# Revit family: Domotics-DomesticRanges-GEWISS-CHORUS_POWER-SOCKET-OUTLET_USA
name_source: partatom
category: Apparecchi elettrici
revit_build: Autodesk Revit 2016 (Build: 20161004_0715(x64)
units: mm (PartAtom-declared; Revit-internal decimal feet)

## family parameters
Condiviso = Sì
Host = Superficie
Mantenere orientamento annotazione = Sì
Punto di calcolo locali = Sì
Quota connettore circolare = Usa diametro
Taglio con vuoti quando caricato = Sì
Tipo di parte = Normale

## types (3) — shared parameters
Breaking capacity: = 1.25 In (100 position changes)
Carico apparente = 0 VA
Catalogue = DOMOTICS
Catalogue Range = CHORUS - DOMESTIC RANGE
Category = Socket-outlet
Description. = Socket-outlet
Description: = 2P+E - 15A
Electrocod = 0131
For plug pins = Flat parallel horizontal
Glow Wire Test = 850°C
IDF = 0721d703-e534-47c8-87a0-3fb374cf64be
IDT = 93e3ec76-1543-4b5d-bb69-3c207991c956
Immagine tipo = GW14286.jpg
Insulation resistance = > 5 MOhm
N. poli = 1
No. Chorus modules = 1
No. Chorus modules: = 1
Produttore = GEWISS S.p.A.
Prolonged operation (no.of position changes) = 10.000 at In 250 V ac cosÃ˜=0,8
Prospetto di default = 1219 mm
Resistance at test voltage = 2000 V at 50 Hz for 1 minute
SEO = Socket outlet
Standard = USA
Standard: = USA
Standard; = IEC 60884-1
TXT ELETTRICO = 15
Technical sheet = https://www.gewiss.com
Terminal grip on cable traction = > 50 N
Terminal tightening capacity flexible cables (mm2) = min. 0,75 - max. 2x4
Terminal tightening capacity rigid cables (mm2) = min. 0,5 - max. 2x2,5
Thermo-pressure with ball = 125
Tipo = CHORUS PRESE USA_GENERICO : GW14286 Presa 1M 2P+T 15A standard USA titanio
URL = https://www.gewiss.com
Version file RFA = 19.0
Volt = 230 V
Voltage = 250/125V AC
Voltage: = 250/125V AC
Wiring terminals = With screw

## per-type parameters (varying)
| type | Colour | Descrizione | EAN code | Modello |
| GW10286 - Socket outlet 1M 2P+T 15A USA standard White | White | S. OUTLET 1M 2P+E 15A USA WHITE | 8011564258259 | GW10286 |
| GW14286 - Socket outlet 1M 2P+T 15A USA standard Titanium | Titanium | SOCKET 1M 2P+E 15A USA STANDARD TITANIUM | 8011564266414 | GW14286 |
| GW12286 - Socket outlet 1M 2P+T 15A USA standard Black | Black | SOCKET 1M 2P+E 15A USA STANDARD BLACK | 8011564267176 | GW12286 |

note: source unit labels omitted for Thermo-pressure with ball — the stored unit's dimension contradicts the parameter name (converter mislabeling)

## geometry (parser evidence)
native form markers: Sweep x2
no freeform markers — native parametric forms only
